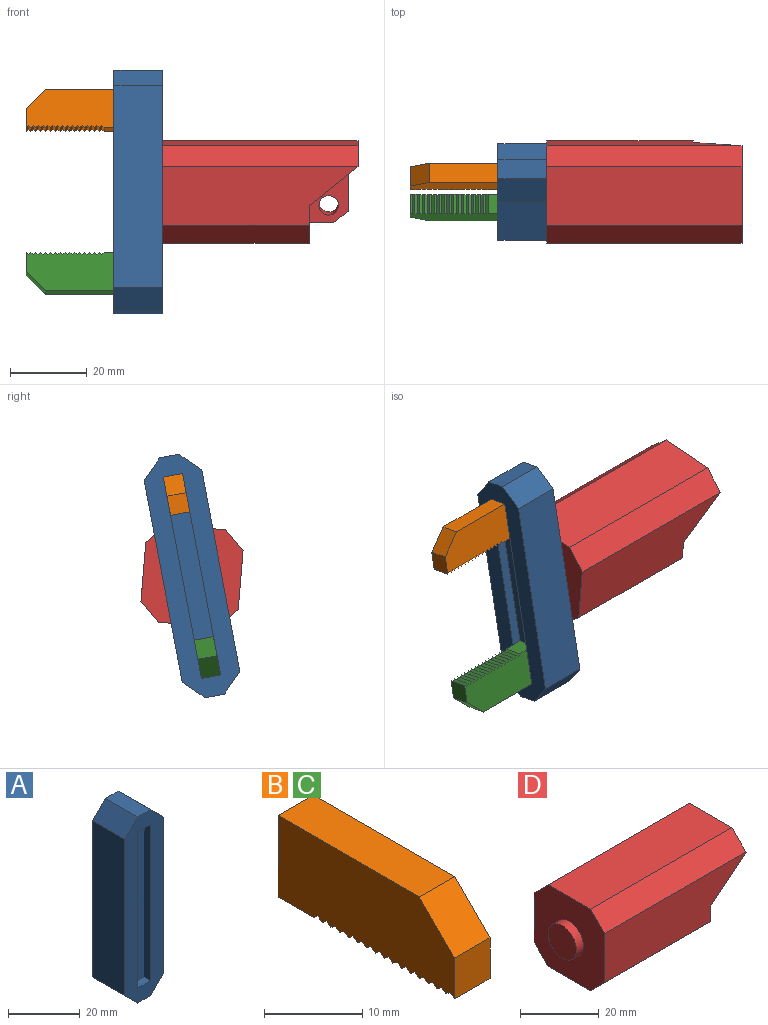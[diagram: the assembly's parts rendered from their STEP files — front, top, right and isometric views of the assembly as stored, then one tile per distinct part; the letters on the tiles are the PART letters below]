
ASSEMBLY  parts=4 mates=4
PART A: 17 faces, bbox 15.2x12.7x63.5 mm
  f0: plane 63.5x15.24mm, normal (0,-1,0), area 645.2mm2, adj f1,f2,f3,f4,f6,f7,f8,f9
  f1: plane 12.7x5.08mm, normal (0,0,1), area 64.5mm2, adj f0,f5,f7,f9
  f2: plane 53.34x12.7mm, normal (-1,0,0), area 677.4mm2, adj f0,f5,f8,f9
  f3: plane 12.7x5.08mm, normal (0,0,-1), area 64.5mm2, adj f0,f5,f6,f8
  f4: plane 53.34x12.7mm, normal (1,0,0), area 677.4mm2, adj f0,f5,f6,f7
  f5: plane 63.5x15.24mm, normal (0,1,0), area 835.1mm2, adj f1,f2,f3,f4,f6,f7,f8,f9
  f6: plane 12.7x5.08mm, normal (0.71,0,-0.71), area 91.2mm2, adj f0,f3,f4,f5
  f7: plane 12.7x5.08mm, normal (0.71,0,0.71), area 91.2mm2, adj f0,f1,f4,f5
  f8: plane 12.7x5.08mm, normal (-0.71,0,-0.71), area 91.2mm2, adj f0,f2,f3,f5
  f9: plane 12.7x5.08mm, normal (-0.71,0,0.71), area 91.2mm2, adj f0,f1,f2,f5
  f10: cylinder r=5.08mm len=10.16mm, axis (0,1,0), area 81.1mm2, adj f5,f11
  f11: plane 10.16x10.16mm, normal (0,1,0), area 81.1mm2, adj f10
  f12: plane 5.08x2.54mm, normal (0,0,-1), area 12.9mm2, adj f0,f13,f15,f16
  f13: plane 53.34x2.54mm, normal (1,0,0), area 135.5mm2, adj f0,f12,f14,f16
  f14: plane 5.08x2.54mm, normal (0,0,1), area 12.9mm2, adj f0,f13,f15,f16
  f15: plane 53.34x2.54mm, normal (-1,0,0), area 135.5mm2, adj f0,f12,f14,f16
  f16: plane 53.34x5.08mm, normal (0,-1,0), area 271mm2, adj f12,f13,f14,f15
PART B: 39 faces, bbox 5.1x25.4x10.2 mm
  f0: plane 25.4x10.16mm, normal (-1,0,0), area 240mm2, adj f1,f2,f4,f5,f6,f7,f8,f9
  f1: plane 5.08x5.08mm, normal (0,0,-1), area 25.8mm2, adj f0,f3,f5,f7
  f2: plane 20.32x5.08mm, normal (0,0,1), area 103.2mm2, adj f0,f3,f5,f6
  f3: plane 25.4x10.16mm, normal (1,0,0), area 240mm2, adj f1,f2,f4,f5,f6,f7,f8,f9
  f4: plane 5.08x5.08mm, normal (0,-1,0), area 25.8mm2, adj f0,f3,f6,f38
  f5: plane 10.16x5.08mm, normal (0,1,0), area 51.6mm2, adj f0,f1,f2,f3
  f6: plane 5.08x5.08mm, normal (0,-0.71,0.71), area 36.5mm2, adj f0,f2,f3,f4
  f7: plane 5.08x0.64mm, normal (0,-0.62,-0.78), area 4.1mm2, adj f0,f1,f3,f8
  f8: plane 5.08x0.64mm, normal (0,0.62,-0.78), area 4.1mm2, adj f0,f3,f7,f35
  f9: plane 5.08x0.64mm, normal (0,-0.62,-0.78), area 4.1mm2, adj f0,f3,f10,f36
  f10: plane 5.08x0.64mm, normal (0,0.62,-0.78), area 4.1mm2, adj f0,f3,f9,f33
  f11: plane 5.08x0.64mm, normal (0,-0.62,-0.78), area 4.1mm2, adj f0,f3,f12,f34
  f12: plane 5.08x0.64mm, normal (0,0.62,-0.78), area 4.1mm2, adj f0,f3,f11,f31
  f13: plane 5.08x0.64mm, normal (0,-0.62,-0.78), area 4.1mm2, adj f0,f3,f14,f32
  f14: plane 5.08x0.64mm, normal (0,0.62,-0.78), area 4.1mm2, adj f0,f3,f13,f29
  f15: plane 5.08x0.64mm, normal (0,-0.62,-0.78), area 4.1mm2, adj f0,f3,f16,f30
  f16: plane 5.08x0.64mm, normal (0,0.62,-0.78), area 4.1mm2, adj f0,f3,f15,f27
  f17: plane 5.08x0.64mm, normal (0,-0.62,-0.78), area 4.1mm2, adj f0,f3,f18,f28
  f18: plane 5.08x0.64mm, normal (0,0.62,-0.78), area 4.1mm2, adj f0,f3,f17,f25
  f19: plane 5.08x0.64mm, normal (0,-0.62,-0.78), area 4.1mm2, adj f0,f3,f20,f26
  f20: plane 5.08x0.64mm, normal (0,0.62,-0.78), area 4.1mm2, adj f0,f3,f19,f23
  f21: plane 5.08x0.64mm, normal (0,-0.62,-0.78), area 4.1mm2, adj f0,f3,f22,f24
  f22: plane 5.08x0.64mm, normal (0,0.62,-0.78), area 4.1mm2, adj f0,f3,f21,f37
  f23: plane 5.08x0.64mm, normal (0,-0.62,-0.78), area 4.1mm2, adj f0,f3,f20,f24
  f24: plane 5.08x0.64mm, normal (0,0.62,-0.78), area 4.1mm2, adj f0,f3,f21,f23
  f25: plane 5.08x0.64mm, normal (0,-0.62,-0.78), area 4.1mm2, adj f0,f3,f18,f26
  f26: plane 5.08x0.64mm, normal (0,0.62,-0.78), area 4.1mm2, adj f0,f3,f19,f25
  f27: plane 5.08x0.64mm, normal (0,-0.62,-0.78), area 4.1mm2, adj f0,f3,f16,f28
  f28: plane 5.08x0.64mm, normal (0,0.62,-0.78), area 4.1mm2, adj f0,f3,f17,f27
  f29: plane 5.08x0.64mm, normal (0,-0.62,-0.78), area 4.1mm2, adj f0,f3,f14,f30
  f30: plane 5.08x0.64mm, normal (0,0.62,-0.78), area 4.1mm2, adj f0,f3,f15,f29
  f31: plane 5.08x0.64mm, normal (0,-0.62,-0.78), area 4.1mm2, adj f0,f3,f12,f32
  f32: plane 5.08x0.64mm, normal (0,0.62,-0.78), area 4.1mm2, adj f0,f3,f13,f31
  f33: plane 5.08x0.64mm, normal (0,-0.62,-0.78), area 4.1mm2, adj f0,f3,f10,f34
  f34: plane 5.08x0.64mm, normal (0,0.62,-0.78), area 4.1mm2, adj f0,f3,f11,f33
  f35: plane 5.08x0.64mm, normal (0,-0.62,-0.78), area 4.1mm2, adj f0,f3,f8,f36
  f36: plane 5.08x0.64mm, normal (0,0.62,-0.78), area 4.1mm2, adj f0,f3,f9,f35
  f37: plane 5.08x0.64mm, normal (0,-0.62,-0.78), area 4.1mm2, adj f0,f3,f22,f38
  f38: plane 5.08x0.64mm, normal (0,0.62,-0.78), area 4.1mm2, adj f0,f3,f4,f37
PART C: same geometry as B
PART D: 20 faces, bbox 53.3x25.4x25.4 mm
  f0: plane 25.4x10.16mm, normal (1,0,0), area 180.6mm2, adj f1,f4,f6,f7,f8,f9,f13,f16
  f1: plane 25.4x12.7mm, normal (0.62,0,-0.78), area 280.9mm2, adj f0,f5,f6,f7,f12,f16,f17
  f2: plane 50.8x15.24mm, normal (0,0,1), area 774.2mm2, adj f3,f5,f10,f11
  f3: plane 25.4x25.4mm, normal (-1,0,0), area 512.5mm2, adj f2,f4,f6,f7,f8,f9,f10,f11
  f4: plane 38.1x15.24mm, normal (0,0,-1), area 580.6mm2, adj f0,f3,f8,f9
  f5: plane 25.4x5.08mm, normal (1,0,0), area 103.2mm2, adj f1,f2,f10,f11
  f6: plane 50.8x15.24mm, normal (0,-1,0), area 645.2mm2, adj f0,f1,f3,f8,f11
  f7: plane 50.8x15.24mm, normal (0,1,0), area 645.2mm2, adj f0,f1,f3,f9,f10
  f8: plane 38.1x5.08mm, normal (0,-0.71,-0.71), area 273.7mm2, adj f0,f3,f4,f6
  f9: plane 38.1x5.08mm, normal (0,0.71,-0.71), area 273.7mm2, adj f0,f3,f4,f7
  f10: plane 50.8x5.08mm, normal (0,0.71,0.71), area 365mm2, adj f2,f3,f5,f7
  f11: plane 50.8x5.08mm, normal (0,-0.71,0.71), area 365mm2, adj f2,f3,f5,f6
  f12: plane 10.16x10.16mm, normal (1,0,0), area 103.2mm2, adj f1,f15,f16,f17
  f13: plane 10.16x6.35mm, normal (0,0,-1), area 64.5mm2, adj f0,f15,f16,f17
  f14: cylinder r=2.54mm len=10.16mm, axis (0,1,0), area 162.1mm2, adj f16,f17
  f15: plane 10.16x3.81mm, normal (0.62,0,-0.78), area 49.6mm2, adj f12,f13,f16,f17
  f16: plane 13.21x10.16mm, normal (0,-1,0), area 66.8mm2, adj f0,f1,f12,f13,f14,f15
  f17: plane 13.21x10.16mm, normal (0,1,0), area 66.8mm2, adj f0,f1,f12,f13,f14,f15
  f18: cylinder r=5.08mm len=10.16mm, axis (1,0,0), area 81.1mm2, adj f3,f19
  f19: plane 10.16x10.16mm, normal (-1,0,0), area 81.1mm2, adj f18
PLACE A rot(axis=(0.71,0.71,-0.07),172.4deg) t=(-26.05,17.8,40.53)mm fixed
PLACE B rot(axis=(-0.09,-0.09,-0.99),90.5deg) t=(-36.21,15.79,38.01)mm
PLACE C rot(axis=(0.71,0.71,-0.07),172.4deg) t=(-36.21,-6.99,-16.49)mm
PLACE D rot(axis=(1,0,0),4.7deg) t=(-7.34,5.45,-1.9)mm
MATE slider C.f2 <-> A.f12  axis (0,-0.19,-0.98) through (-36.21,-0.57,-15.44)mm
MATE parallel B.f1 <-> C.f1  axis (0,-0.19,-0.98) through (-38.75,7.47,26.98)mm
MATE slider B.f2 <-> A.f14  axis (0,0.19,0.98) through (-36.21,9.37,36.96)mm
MATE revolute A.f10 <-> D.f18  axis (1,0,0) through (-28.59,4.4,10.76)mm
